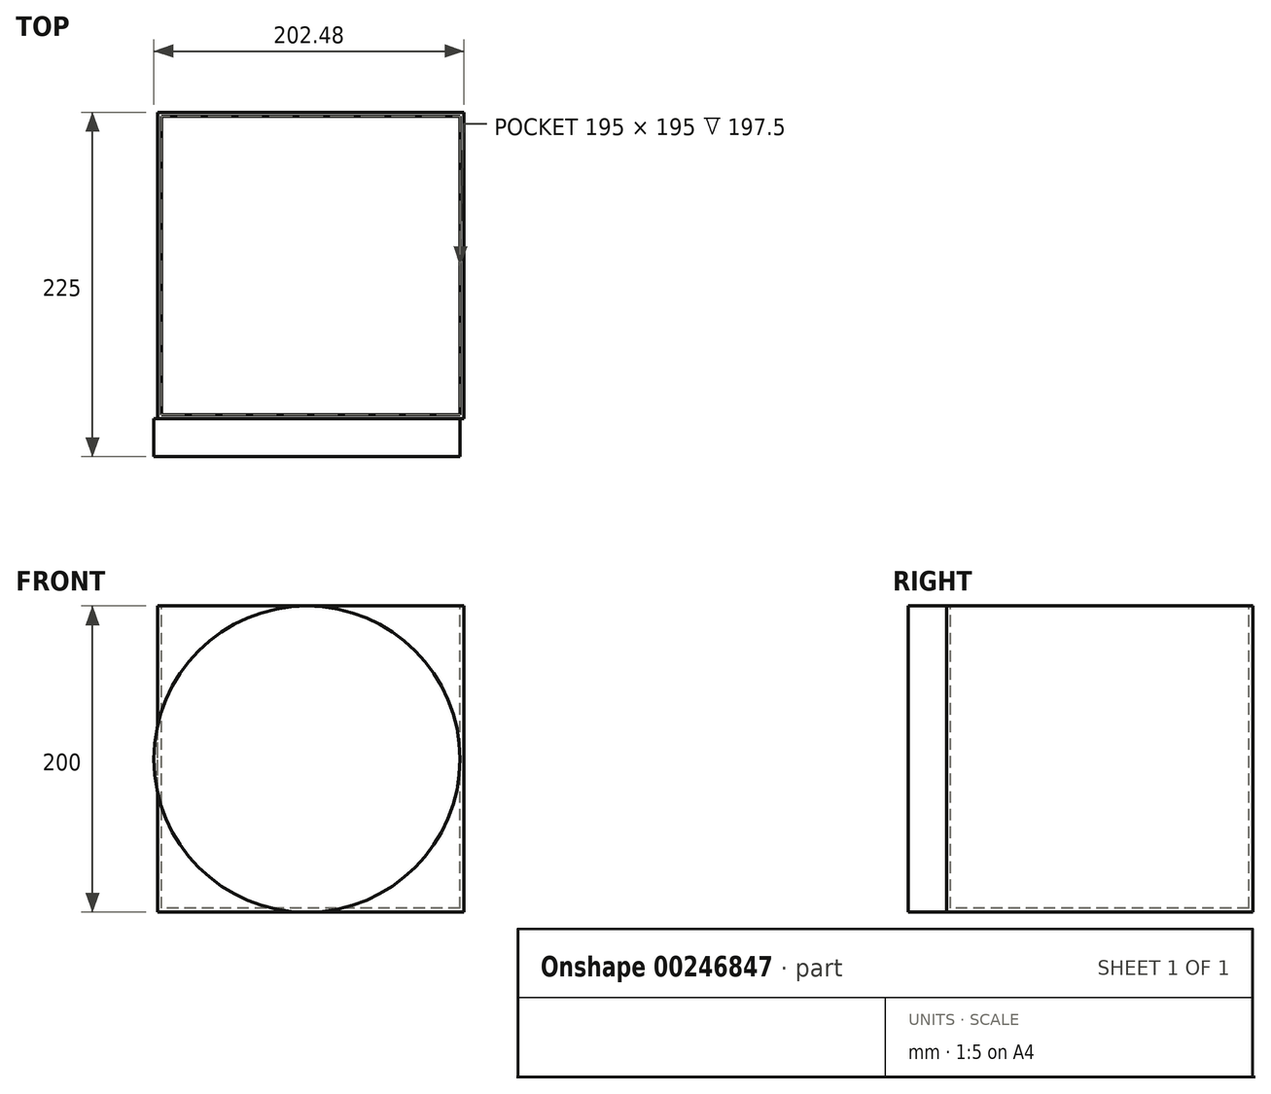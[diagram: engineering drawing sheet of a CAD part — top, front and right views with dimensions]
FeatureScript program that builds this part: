
annotation { "Feature Type Name" : "Feature", "Feature Type Description" : "" }
export const myFeature = defineFeature(function(context is Context, id is Id, definition is map)
    precondition{}
    {
        {
            var Q0;
            Q0=qCreatedBy(makeId("Front.planeOp"),FACE);
            var sketch = newSketch(context, id + "F0", { "sketchPlane" : qUnion([Q0])});
            skLineSegment(sketch, "E0.bottom", {"start": v(102.48, -100) * mm, "end": v(-97.52, -100) * mm});
            skLineSegment(sketch, "E0.top", {"start": v(102.48, 100) * mm, "end": v(-97.52, 100) * mm});
            skLineSegment(sketch, "E0.left", {"start": v(102.48, -100) * mm, "end": v(102.48, 100) * mm});
            skLineSegment(sketch, "E0.right", {"start": v(-97.52, -100) * mm, "end": v(-97.52, 100) * mm});
            skPoint(sketch, "E0.middle", {"position": v(2.48, 0) * mm});
            skSolve(sketch);
        }
        {
            var Q0;
            Q0=makeQuery(id+"F0.imprint","IMPRINT",FACE,{"disambiguationData":[TD([[makeQuery(id+"F0.imprint","IMPRINT",EDGE,{"derivedFrom":sQuery(id+"F0.wireOp",EDGE,"E0.bottom")}),-1.0]])]});
            extrude(context, id + "F1", {"entities" : qUnion([Q0]), "oppositeDirection" : true, "depth" : 200 * mm});
        }
        {
            var Q0;
            Q0=makeQuery(id+"F1.opExtrude","CAP_FACE",FACE,{"disambiguationData":[OSD([sQuery(id+"F0.wireOp",EDGE,"E0.bottom"),sQuery(id+"F0.wireOp",EDGE,"E0.top"),sQuery(id+"F0.wireOp",EDGE,"E0.left"),sQuery(id+"F0.wireOp",EDGE,"E0.right")])],"isStart":true});
            var sketch = newSketch(context, id + "F2", { "sketchPlane" : qUnion([Q0])});
            skArc(sketch, "E1", {"start": v(-97.52, 100) * mm, "mid": v(2.48, 53.68) * mm, "end": v(102.48, 100) * mm});
            skPoint(sketch, "E1.first.point", {"position": v(-97.52, 100) * mm});
            skPoint(sketch, "E1.second.point", {"position": v(102.48, 100) * mm});
            skPoint(sketch, "E1.third.point", {"position": v(131.38, 208.74) * mm});
            skSolve(sketch);
        }
        {
            var Q0;
            Q0=sQuery(id+"F2.wireOp",EDGE,"E1");
            extrude(context, id + "F3", {"bodyType" : ToolBodyType.SURFACE, "surfaceEntities" : qUnion([Q0]), "oppositeDirection" : true, "depth" : 200 * mm});
        }
        {
            var Q0;
            Q0=makeQuery(id+"F1.opExtrude","SWEPT_FACE",FACE,{"disambiguationData":[OSD([sQuery(id+"F0.wireOp",EDGE,"E0.top")])]});
            shell(context, id + "F4", {"entities" : qUnion([Q0]), "thickness" : 2.5 * mm});
        }
        {
            var Q0;
            Q0=makeQuery(id+"F1.opExtrude","CAP_FACE",FACE,{"disambiguationData":[OSD([sQuery(id+"F0.wireOp",EDGE,"E0.bottom"),sQuery(id+"F0.wireOp",EDGE,"E0.top"),sQuery(id+"F0.wireOp",EDGE,"E0.left"),sQuery(id+"F0.wireOp",EDGE,"E0.right")])],"isStart":true});
            var sketch = newSketch(context, id + "F5", { "sketchPlane" : qUnion([Q0])});
            skCircle(sketch, "E2", {"center": v(0, 0) * mm, "radius": 100 * mm});
            skSolve(sketch);
        }
        {
            var Q0;
            Q0 = qSketchRegion(id + "F5", true);
            extrude(context, id + "F6", {"entities" : qUnion([Q0]), "operationType" : NewBodyOperationType.ADD, "depth" : 25 * mm});
        }
    });
